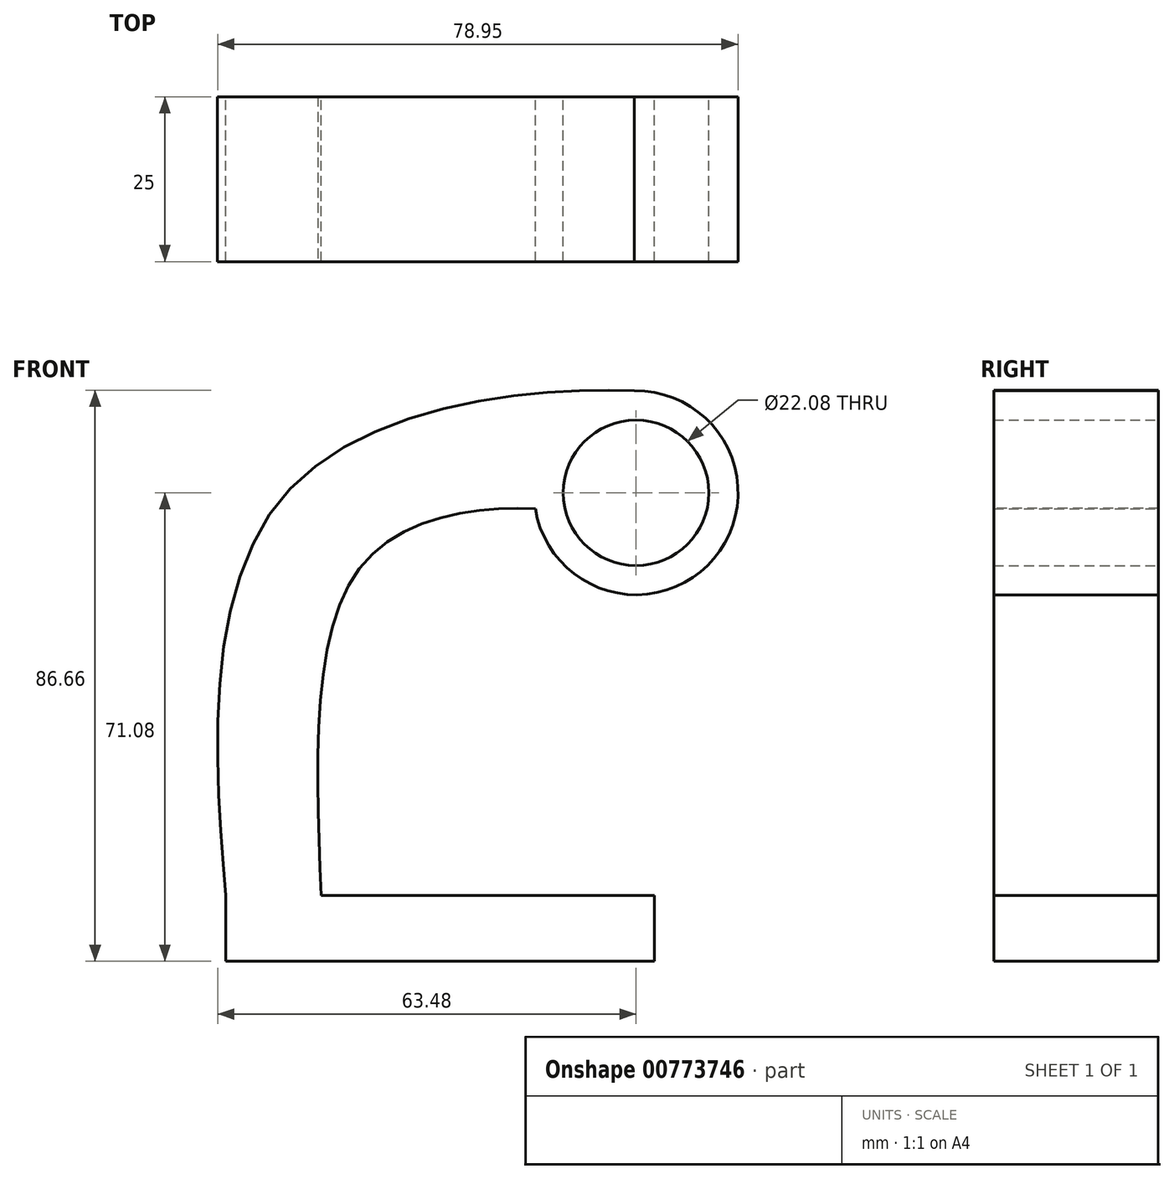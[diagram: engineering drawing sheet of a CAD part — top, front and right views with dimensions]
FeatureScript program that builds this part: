
annotation { "Feature Type Name" : "Feature", "Feature Type Description" : "" }
export const myFeature = defineFeature(function(context is Context, id is Id, definition is map)
    precondition{}
    {
        {
            var Q0;
            Q0=qCreatedBy(makeId("Front.planeOp"),FACE);
            var sketch = newSketch(context, id + "F0", { "sketchPlane" : qUnion([Q0])});
            skCircle(sketch, "E0", {"center": v(0, 0) * mm, "radius": 15.47 * mm});
            skFitSpline(sketch, "E1", {"points": [v(-0.24, 15.46) * mm, v(-53.05, 0) * mm, v(-62.22, -61.08) * mm], "startDerivative": vector(-83.28, 4.22) * mm, "endDerivative": vector(8.76, -104.33) * mm});
            skLineSegment(sketch, "E2.bottom", {"start": v(-62.22, -61.08) * mm, "end": v(2.78, -61.08) * mm});
            skLineSegment(sketch, "E2.top", {"start": v(-62.22, -71.08) * mm, "end": v(2.78, -71.08) * mm});
            skLineSegment(sketch, "E2.left", {"start": v(-62.22, -61.08) * mm, "end": v(-62.22, -71.08) * mm});
            skLineSegment(sketch, "E2.right", {"start": v(2.78, -61.08) * mm, "end": v(2.78, -71.08) * mm});
            skCircle(sketch, "E3", {"center": v(0, 0) * mm, "radius": 11.04 * mm});
            skFitSpline(sketch, "E4", {"points": [v(-15.28, -2.39) * mm, v(-41.56, -10.98) * mm, v(-47.8, -61.08) * mm], "startDerivative": vector(-60.75, 2.16) * mm, "endDerivative": vector(3.05, -94.54) * mm});
            skPoint(sketch, "E5", {"position": v(2310.39, 1793.37) * mm});
            skSolve(sketch);
        }
        {
            var Q0;
            Q0 = qSketchRegion(id + "F0", true);
            extrude(context, id + "F1", {"entities" : qUnion([Q0]), "depth" : 25 * mm, "offsetDistance" : 25 * mm});
        }
    });
